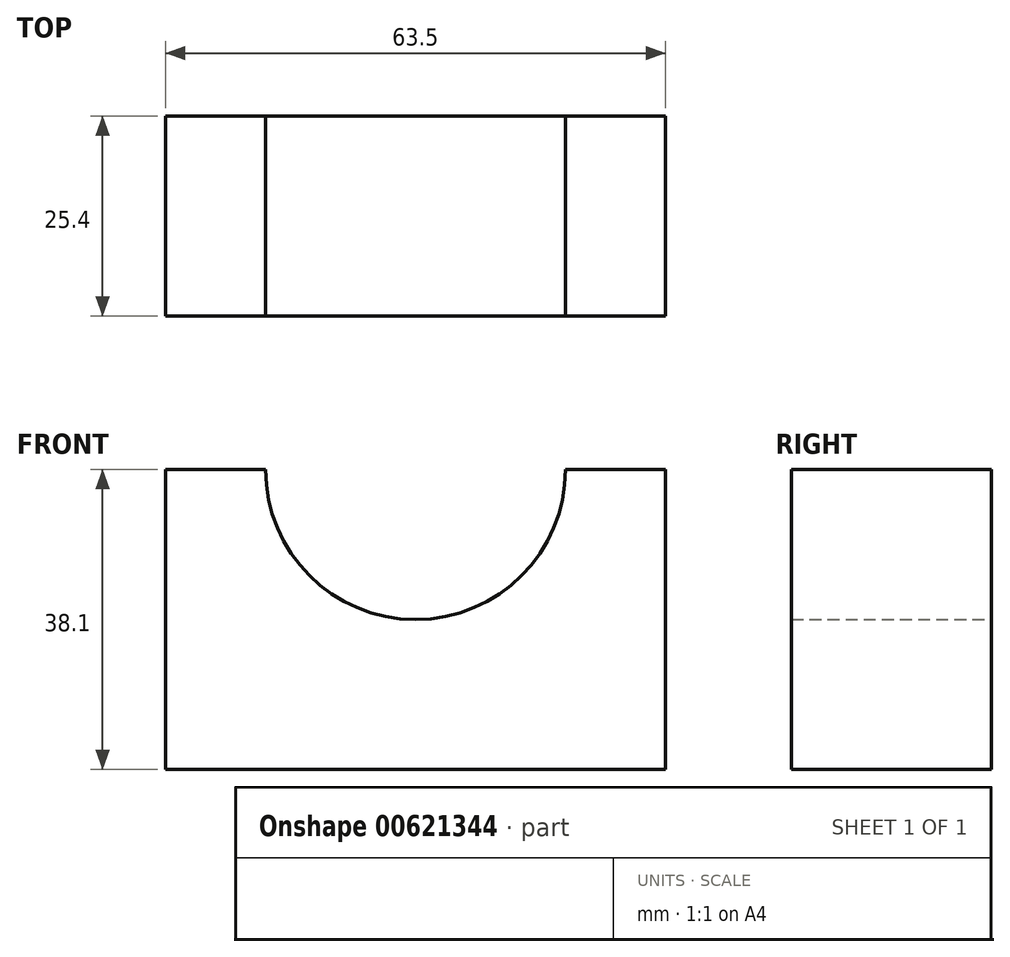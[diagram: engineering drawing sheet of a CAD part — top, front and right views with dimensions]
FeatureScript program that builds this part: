
annotation { "Feature Type Name" : "Feature", "Feature Type Description" : "" }
export const myFeature = defineFeature(function(context is Context, id is Id, definition is map)
    precondition{}
    {
        {
            var Q0;
            Q0=qCreatedBy(makeId("Front.planeOp"),FACE);
            var sketch = newSketch(context, id + "F0", { "sketchPlane" : qUnion([Q0])});
            skLineSegment(sketch, "E0", {"start": v(0, 38.1) * mm, "end": v(0, 0) * mm});
            skLineSegment(sketch, "E1", {"start": v(0, 0) * mm, "end": v(63.5, 0) * mm});
            skLineSegment(sketch, "E2", {"start": v(63.5, 0) * mm, "end": v(63.5, 38.1) * mm});
            skLineSegment(sketch, "E3", {"start": v(0, 38.1) * mm, "end": v(12.7, 38.1) * mm});
            skLineSegment(sketch, "E4", {"start": v(63.5, 38.1) * mm, "end": v(50.8, 38.1) * mm});
            skArc(sketch, "E5", {"start": v(12.7, 38.1) * mm, "mid": v(31.75, 19.05) * mm, "end": v(50.8, 38.1) * mm});
            skSolve(sketch);
        }
        {
            var Q0;
            Q0=makeQuery(id+"F0.imprint","IMPRINT",FACE,{"disambiguationData":[TD([[makeQuery(id+"F0.imprint","IMPRINT",EDGE,{"derivedFrom":sQuery(id+"F0.wireOp",EDGE,"E0")}),1.0]])]});
            extrude(context, id + "F1", {"entities" : qUnion([Q0]), "depth" : 25.4 * mm, "offsetDistance" : 25.4 * mm});
        }
    });
